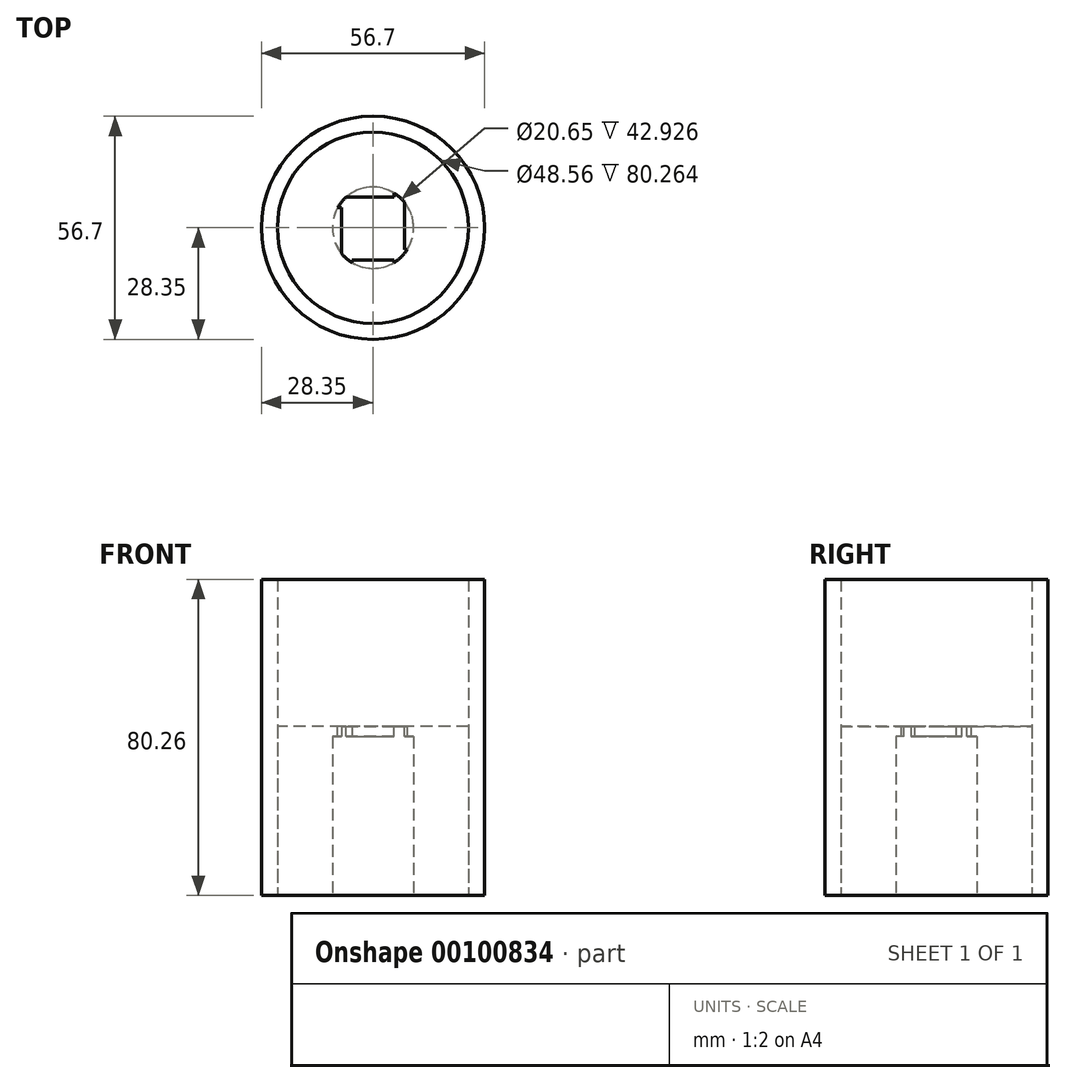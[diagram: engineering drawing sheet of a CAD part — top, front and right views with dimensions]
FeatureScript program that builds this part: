
annotation { "Feature Type Name" : "Feature", "Feature Type Description" : "" }
export const myFeature = defineFeature(function(context is Context, id is Id, definition is map)
    precondition{}
    {
        {
            var Q0;
            Q0=qCreatedBy(makeId("Top.planeOp"),FACE);
            var sketch = newSketch(context, id + "F0", { "sketchPlane" : qUnion([Q0])});
            skCircle(sketch, "E0", {"center": v(0, 0) * mm, "radius": 10.33 * mm});
            skCircle(sketch, "E1", {"center": v(0, 0) * mm, "radius": 28.35 * mm});
            skCircle(sketch, "E2", {"center": v(0, 0) * mm, "radius": 24.28 * mm});
            skSolve(sketch);
        }
        {
            var Q0;
            Q0 = qSketchRegion(id + "F0", true);
            extrude(context, id + "F1", {"entities" : qUnion([Q0]), "depth" : 80.26 * mm});
        }
        {
            var Q0;
            Q0=makeQuery(id+"F0.imprint","IMPRINT",FACE,{"disambiguationData":[TD([[makeQuery(id+"F0.imprint","IMPRINT",EDGE,{"derivedFrom":sQuery(id+"F0.wireOp",EDGE,"E0")}),-1.0]])]});
            extrude(context, id + "F2", {"entities" : qUnion([Q0]), "depth" : 42.93 * mm});
        }
        {
            var Q0;
            Q0=makeQuery(id+"F2.opExtrude","CAP_FACE",FACE,{"disambiguationData":[OSD([sQuery(id+"F0.wireOp",EDGE,"E0"),sQuery(id+"F0.wireOp",EDGE,"E2")])],"isStart":false});
            var sketch = newSketch(context, id + "F3", { "sketchPlane" : qUnion([Q0])});
            skLineSegment(sketch, "E3.bottom", {"start": v(-6.78, 7.79) * mm, "end": v(5.32, 7.79) * mm});
            skLineSegment(sketch, "E3.top", {"start": v(-6.78, 10.79) * mm, "end": v(5.32, 10.79) * mm});
            skLineSegment(sketch, "E3.left", {"start": v(-6.78, 7.79) * mm, "end": v(-6.78, 10.79) * mm});
            skLineSegment(sketch, "E3.right", {"start": v(5.32, 7.79) * mm, "end": v(5.32, 10.79) * mm});
            skLineSegment(sketch, "E4", {"start": v(-55.13, 0) * mm, "end": v(42.25, 0) * mm});
            skLineSegment(sketch, "E5.MirrorCS", {"start": v(-6.78, -7.79) * mm, "end": v(5.32, -7.79) * mm});
            skLineSegment(sketch, "E6.MirrorCS", {"start": v(5.32, -7.79) * mm, "end": v(5.32, -10.79) * mm});
            skLineSegment(sketch, "E7.MirrorCS", {"start": v(-6.78, -7.79) * mm, "end": v(-6.78, -10.79) * mm});
            skLineSegment(sketch, "E8.MirrorCS", {"start": v(-6.78, -10.79) * mm, "end": v(5.32, -10.79) * mm});
            skLineSegment(sketch, "E9.1.0", {"start": v(-0.23, -55.36) * mm, "end": v(-0.23, 42.02) * mm});
            skLineSegment(sketch, "E9.1.1", {"start": v(-8.01, -7) * mm, "end": v(-8.01, 5.1) * mm});
            skLineSegment(sketch, "E9.1.2", {"start": v(-11.01, -7) * mm, "end": v(-11.01, 5.1) * mm});
            skLineSegment(sketch, "E9.1.3", {"start": v(-8.01, -7) * mm, "end": v(-11.01, -7) * mm});
            skLineSegment(sketch, "E9.1.4", {"start": v(-8.01, 5.1) * mm, "end": v(-11.01, 5.1) * mm});
            skLineSegment(sketch, "E9.2.0", {"start": v(55.13, -0.45) * mm, "end": v(-42.25, -0.45) * mm});
            skLineSegment(sketch, "E9.2.1", {"start": v(6.78, -8.24) * mm, "end": v(-5.32, -8.24) * mm});
            skLineSegment(sketch, "E9.2.2", {"start": v(6.78, -11.24) * mm, "end": v(-5.32, -11.24) * mm});
            skLineSegment(sketch, "E9.2.3", {"start": v(6.78, -8.24) * mm, "end": v(6.78, -11.24) * mm});
            skLineSegment(sketch, "E9.2.4", {"start": v(-5.32, -8.24) * mm, "end": v(-5.32, -11.24) * mm});
            skLineSegment(sketch, "E9.3.0", {"start": v(0.23, 54.9) * mm, "end": v(0.23, -42.47) * mm});
            skLineSegment(sketch, "E9.3.1", {"start": v(8.01, 6.56) * mm, "end": v(8.01, -5.55) * mm});
            skLineSegment(sketch, "E9.3.2", {"start": v(11.01, 6.56) * mm, "end": v(11.01, -5.55) * mm});
            skLineSegment(sketch, "E9.3.3", {"start": v(8.01, 6.56) * mm, "end": v(11.01, 6.56) * mm});
            skLineSegment(sketch, "E9.3.4", {"start": v(8.01, -5.55) * mm, "end": v(11.01, -5.55) * mm});
            skPoint(sketch, "E9.center", {"position": v(0, -0.23) * mm});
            skSolve(sketch);
        }
        {
            var Q0;
            {var subQ3=sQuery(id+"F3.wireOp",EDGE,"E9.3.0");var subQ5=sQuery(id+"F3.wireOp",EDGE,"E3.top");var subQ7=makeQuery(id+"F3.imprint","INTERSECT",VERTEX,{"derivedFrom":[subQ5,subQ3]});Q0=makeQuery(id+"F3.imprint","IMPRINT",FACE,{"disambiguationData":[TD([[makeQuery(id+"F3.imprint","IMPRINT",EDGE,{"disambiguationData":[TD([[subQ7,1.0]])],"derivedFrom":subQ5}),-1.0]])]});}
            var Q1;
            {var subQ1=sQuery(id+"F3.wireOp",EDGE,"E3.bottom");var subQ5=sQuery(id+"F3.wireOp",EDGE,"E3.right");var subQ6=makeQuery(id+"F3.imprint","INTERSECT",VERTEX,{"derivedFrom":[subQ1,subQ5]});Q1=makeQuery(id+"F3.imprint","IMPRINT",FACE,{"disambiguationData":[TD([[makeQuery(id+"F3.imprint","IMPRINT",EDGE,{"disambiguationData":[TD([[subQ6,1.0]])],"derivedFrom":subQ1}),1.0]])]});}
            var Q2;
            {var subQ0=sQuery(id+"F3.wireOp",EDGE,"E9.3.2");var subQ1=sQuery(id+"F3.wireOp",EDGE,"E9.2.0");var subQ2=makeQuery(id+"F3.imprint","INTERSECT",VERTEX,{"derivedFrom":[subQ1,subQ0]});Q2=makeQuery(id+"F3.imprint","IMPRINT",FACE,{"disambiguationData":[TD([[makeQuery(id+"F3.imprint","IMPRINT",EDGE,{"disambiguationData":[TD([[subQ2,-1.0]])],"derivedFrom":subQ1}),-1.0]])]});}
            var Q3;
            {var subQ5=sQuery(id+"F3.wireOp",EDGE,"E9.3.2");var subQ7=sQuery(id+"F3.wireOp",EDGE,"E9.2.0");var subQ8=makeQuery(id+"F3.imprint","INTERSECT",VERTEX,{"derivedFrom":[subQ7,subQ5]});Q3=makeQuery(id+"F3.imprint","IMPRINT",FACE,{"disambiguationData":[TD([[makeQuery(id+"F3.imprint","IMPRINT",EDGE,{"disambiguationData":[TD([[subQ8,-1.0]])],"derivedFrom":subQ7}),1.0]])]});}
            var Q4;
            {var subQ1=sQuery(id+"F3.wireOp",EDGE,"E9.2.1");var subQ7=sQuery(id+"F3.wireOp",EDGE,"E6.MirrorCS");var subQ8=makeQuery(id+"F3.imprint","INTERSECT",VERTEX,{"derivedFrom":[subQ7,subQ1]});Q4=makeQuery(id+"F3.imprint","IMPRINT",FACE,{"disambiguationData":[TD([[makeQuery(id+"F3.imprint","IMPRINT",EDGE,{"disambiguationData":[TD([[subQ8,-1.0]])],"derivedFrom":subQ7}),-1.0]])]});}
            var Q5;
            {var subQ5=sQuery(id+"F3.wireOp",EDGE,"E9.3.0");var subQ7=sQuery(id+"F3.wireOp",EDGE,"E9.2.2");var subQ8=makeQuery(id+"F3.imprint","INTERSECT",VERTEX,{"derivedFrom":[subQ7,subQ5]});Q5=makeQuery(id+"F3.imprint","IMPRINT",FACE,{"disambiguationData":[TD([[makeQuery(id+"F3.imprint","IMPRINT",EDGE,{"disambiguationData":[TD([[subQ8,-1.0]])],"derivedFrom":subQ7}),-1.0]])]});}
            var Q6;
            {var subQ3=sQuery(id+"F3.wireOp",EDGE,"E9.2.0");var subQ5=sQuery(id+"F3.wireOp",EDGE,"E9.1.2");var subQ6=makeQuery(id+"F3.imprint","INTERSECT",VERTEX,{"derivedFrom":[subQ5,subQ3]});Q6=makeQuery(id+"F3.imprint","IMPRINT",FACE,{"disambiguationData":[TD([[makeQuery(id+"F3.imprint","IMPRINT",EDGE,{"disambiguationData":[TD([[subQ6,1.0]])],"derivedFrom":subQ5}),-1.0]])]});}
            var Q7;
            {var subQ1=sQuery(id+"F3.wireOp",EDGE,"E9.1.1");var subQ5=sQuery(id+"F3.wireOp",EDGE,"E9.1.4");var subQ6=makeQuery(id+"F3.imprint","INTERSECT",VERTEX,{"derivedFrom":[subQ1,subQ5]});Q7=makeQuery(id+"F3.imprint","IMPRINT",FACE,{"disambiguationData":[TD([[makeQuery(id+"F3.imprint","IMPRINT",EDGE,{"disambiguationData":[TD([[subQ6,1.0]])],"derivedFrom":subQ1}),1.0]])]});}
            var Q8;
            {var subQ0=sQuery(id+"F3.wireOp",EDGE,"E9.2.0");var subQ1=sQuery(id+"F3.wireOp",EDGE,"E9.1.1");var subQ2=makeQuery(id+"F3.imprint","INTERSECT",VERTEX,{"derivedFrom":[subQ1,subQ0]});Q8=makeQuery(id+"F3.imprint","IMPRINT",FACE,{"disambiguationData":[TD([[makeQuery(id+"F3.imprint","IMPRINT",EDGE,{"disambiguationData":[TD([[subQ2,1.0]])],"derivedFrom":subQ1}),1.0]])]});}
            var Q9;
            {var subQ0=sQuery(id+"F3.wireOp",EDGE,"E9.1.1");var subQ1=sQuery(id+"F3.wireOp",EDGE,"E4");var subQ2=makeQuery(id+"F3.imprint","INTERSECT",VERTEX,{"derivedFrom":[subQ1,subQ0]});Q9=makeQuery(id+"F3.imprint","IMPRINT",FACE,{"disambiguationData":[TD([[makeQuery(id+"F3.imprint","IMPRINT",EDGE,{"disambiguationData":[TD([[subQ2,1.0]])],"derivedFrom":subQ1}),-1.0]])]});}
            var Q10;
            {var subQ0=sQuery(id+"F3.wireOp",EDGE,"E9.3.1");var subQ1=sQuery(id+"F3.wireOp",EDGE,"E4");var subQ2=makeQuery(id+"F3.imprint","INTERSECT",VERTEX,{"derivedFrom":[subQ1,subQ0]});Q10=makeQuery(id+"F3.imprint","IMPRINT",FACE,{"disambiguationData":[TD([[makeQuery(id+"F3.imprint","IMPRINT",EDGE,{"disambiguationData":[TD([[subQ2,-1.0]])],"derivedFrom":subQ1}),-1.0]])]});}
            var Q11;
            {var subQ0=sQuery(id+"F3.wireOp",EDGE,"E9.3.1");var subQ1=sQuery(id+"F3.wireOp",EDGE,"E9.2.0");var subQ2=makeQuery(id+"F3.imprint","INTERSECT",VERTEX,{"derivedFrom":[subQ1,subQ0]});Q11=makeQuery(id+"F3.imprint","IMPRINT",FACE,{"disambiguationData":[TD([[makeQuery(id+"F3.imprint","IMPRINT",EDGE,{"disambiguationData":[TD([[subQ2,1.0]])],"derivedFrom":subQ1}),1.0]])]});}
            var Q12;
            {var subQ0=sQuery(id+"F3.wireOp",EDGE,"E9.3.1");var subQ1=sQuery(id+"F3.wireOp",EDGE,"E4");var subQ2=makeQuery(id+"F3.imprint","INTERSECT",VERTEX,{"derivedFrom":[subQ1,subQ0]});Q12=makeQuery(id+"F3.imprint","IMPRINT",FACE,{"disambiguationData":[TD([[makeQuery(id+"F3.imprint","IMPRINT",EDGE,{"disambiguationData":[TD([[subQ2,-1.0]])],"derivedFrom":subQ1}),1.0]])]});}
            var Q13;
            {var subQ3=sQuery(id+"F3.wireOp",EDGE,"E9.1.0");var subQ5=sQuery(id+"F3.wireOp",EDGE,"E3.top");var subQ6=makeQuery(id+"F3.imprint","INTERSECT",VERTEX,{"derivedFrom":[subQ5,subQ3]});Q13=makeQuery(id+"F3.imprint","IMPRINT",FACE,{"disambiguationData":[TD([[makeQuery(id+"F3.imprint","IMPRINT",EDGE,{"disambiguationData":[TD([[subQ6,1.0]])],"derivedFrom":subQ5}),-1.0]])]});}
            var Q14;
            {var subQ5=sQuery(id+"F3.wireOp",EDGE,"E8.MirrorCS");var subQ7=sQuery(id+"F3.wireOp",EDGE,"E9.1.0");var subQ9=makeQuery(id+"F3.imprint","INTERSECT",VERTEX,{"derivedFrom":[subQ5,subQ7]});Q14=makeQuery(id+"F3.imprint","IMPRINT",FACE,{"disambiguationData":[TD([[makeQuery(id+"F3.imprint","IMPRINT",EDGE,{"disambiguationData":[TD([[subQ9,1.0]])],"derivedFrom":subQ5}),1.0]])]});}
            var Q15;
            {var subQ0=sQuery(id+"F3.wireOp",EDGE,"E9.1.0");var subQ1=sQuery(id+"F3.wireOp",EDGE,"E8.MirrorCS");var subQ2=makeQuery(id+"F3.imprint","INTERSECT",VERTEX,{"derivedFrom":[subQ1,subQ0]});Q15=makeQuery(id+"F3.imprint","IMPRINT",FACE,{"disambiguationData":[TD([[makeQuery(id+"F3.imprint","IMPRINT",EDGE,{"disambiguationData":[TD([[subQ2,-1.0]])],"derivedFrom":subQ1}),1.0]])]});}
            var Q16;
            {var subQ0=sQuery(id+"F3.wireOp",EDGE,"E3.bottom");var subQ3=sQuery(id+"F3.wireOp",EDGE,"E9.1.0");var subQ4=makeQuery(id+"F3.imprint","INTERSECT",VERTEX,{"derivedFrom":[subQ0,subQ3]});Q16=makeQuery(id+"F3.imprint","IMPRINT",FACE,{"disambiguationData":[TD([[makeQuery(id+"F3.imprint","IMPRINT",EDGE,{"disambiguationData":[TD([[subQ4,-1.0]])],"derivedFrom":subQ3}),1.0]])]});}
            var Q17;
            {var subQ0=sQuery(id+"F3.wireOp",EDGE,"E9.1.0");var subQ1=sQuery(id+"F3.wireOp",EDGE,"E3.bottom");var subQ2=makeQuery(id+"F3.imprint","INTERSECT",VERTEX,{"derivedFrom":[subQ1,subQ0]});Q17=makeQuery(id+"F3.imprint","IMPRINT",FACE,{"disambiguationData":[TD([[makeQuery(id+"F3.imprint","IMPRINT",EDGE,{"disambiguationData":[TD([[subQ2,-1.0]])],"derivedFrom":subQ1}),1.0]])]});}
            var Q18;
            {var subQ0=sQuery(id+"F3.wireOp",EDGE,"E9.2.1");var subQ1=sQuery(id+"F3.wireOp",EDGE,"E9.1.0");var subQ2=makeQuery(id+"F3.imprint","INTERSECT",VERTEX,{"derivedFrom":[subQ1,subQ0]});Q18=makeQuery(id+"F3.imprint","IMPRINT",FACE,{"disambiguationData":[TD([[makeQuery(id+"F3.imprint","IMPRINT",EDGE,{"disambiguationData":[TD([[subQ2,1.0]])],"derivedFrom":subQ1}),-1.0]])]});}
            var Q19;
            {var subQ0=sQuery(id+"F3.wireOp",EDGE,"E9.2.1");var subQ1=sQuery(id+"F3.wireOp",EDGE,"E9.1.0");var subQ2=makeQuery(id+"F3.imprint","INTERSECT",VERTEX,{"derivedFrom":[subQ1,subQ0]});Q19=makeQuery(id+"F3.imprint","IMPRINT",FACE,{"disambiguationData":[TD([[makeQuery(id+"F3.imprint","IMPRINT",EDGE,{"disambiguationData":[TD([[subQ2,1.0]])],"derivedFrom":subQ1}),1.0]])]});}
            extrude(context, id + "F4", {"entities" : qUnion([Q0, Q1, Q2, Q3, Q4, Q5, Q6, Q7, Q8, Q9, Q10, Q11, Q12, Q13, Q14, Q15, Q16, Q17, Q18, Q19]), "operationType" : NewBodyOperationType.ADD, "oppositeDirection" : true, "depth" : 2.54 * mm});
        }
    });
